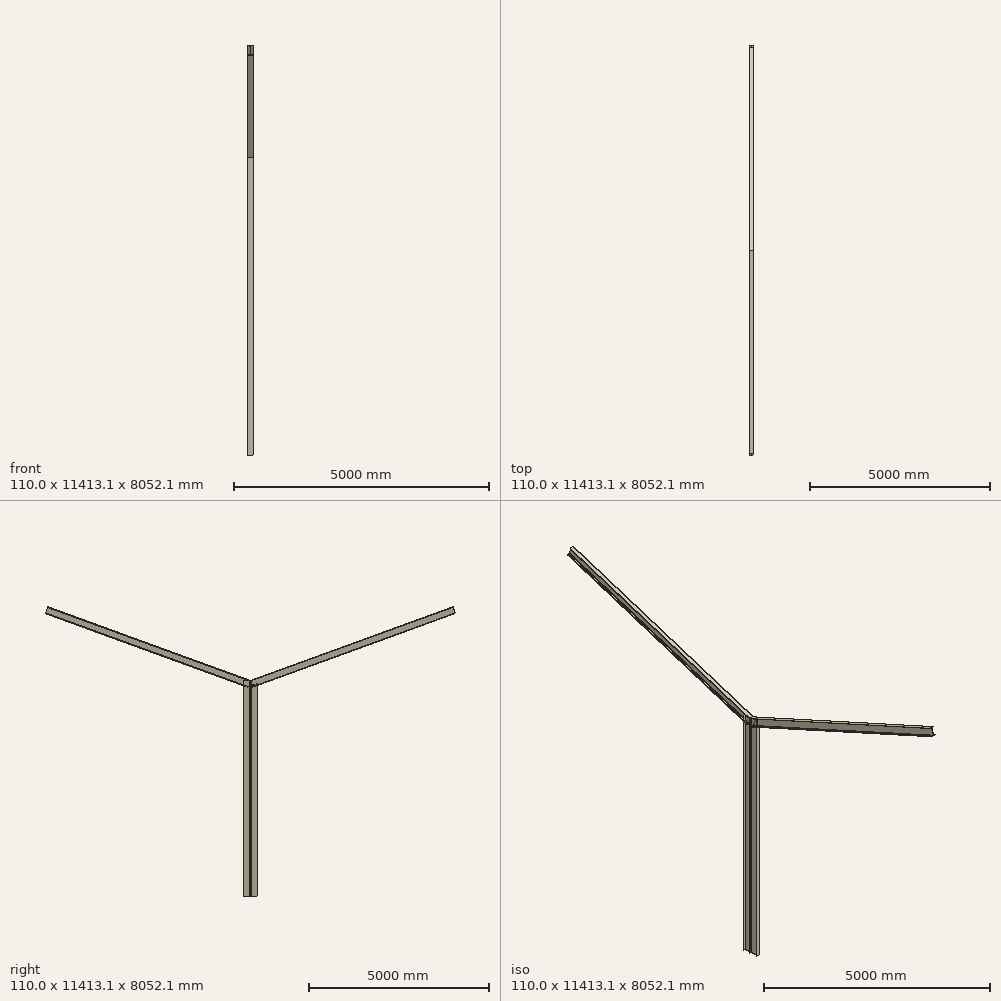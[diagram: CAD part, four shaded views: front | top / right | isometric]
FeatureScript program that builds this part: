
annotation { "Feature Type Name" : "Feature", "Feature Type Description" : "" }
export const myFeature = defineFeature(function(context is Context, id is Id, definition is map)
    precondition{}
    {
        {
            var Q0;
            Q0=qCreatedBy(makeId("Top.planeOp"),FACE);
            var sketch = newSketch(context, id + "F0", { "sketchPlane" : qUnion([Q0])});
            skLineSegment(sketch, "E0.bottom", {"start": v(0, 0) * mm, "end": v(-50, 0) * mm, "construction": true});
            skLineSegment(sketch, "E0.top", {"start": v(0, 100) * mm, "end": v(-55, 100) * mm});
            skLineSegment(sketch, "E0.left", {"start": v(0, 0) * mm, "end": v(0, 100) * mm, "construction": true});
            skLineSegment(sketch, "E0.right", {"start": v(-50, 0) * mm, "end": v(-50, 100) * mm, "construction": true});
            skCircle(sketch, "E1", {"center": v(-50, 100) * mm, "radius": 5 * mm});
            skLineSegment(sketch, "E2", {"start": v(-50.78, 95.06) * mm, "end": v(-9.06, 88.45) * mm});
            skLineSegment(sketch, "E3.MirrorCS", {"start": v(50.78, 95.06) * mm, "end": v(9.06, 88.45) * mm});
            skLineSegment(sketch, "E4.MirrorCS", {"start": v(0, 100) * mm, "end": v(55, 100) * mm});
            skCircle(sketch, "E5.MirrorC", {"center": v(50, 100) * mm, "radius": 5 * mm});
            skLineSegment(sketch, "E6.MirrorCS", {"start": v(-50.78, -95.06) * mm, "end": v(-9.06, -88.45) * mm});
            skLineSegment(sketch, "E7.MirrorCS", {"start": v(0, -100) * mm, "end": v(-55, -100) * mm});
            skLineSegment(sketch, "E8.MirrorCS", {"start": v(0, -100) * mm, "end": v(55, -100) * mm});
            skLineSegment(sketch, "E9.MirrorCS", {"start": v(50.78, -95.06) * mm, "end": v(9.06, -88.45) * mm});
            skCircle(sketch, "E10.MirrorC", {"center": v(-50, -100) * mm, "radius": 5 * mm});
            skCircle(sketch, "E11.MirrorC", {"center": v(50, -100) * mm, "radius": 5 * mm});
            skLineSegment(sketch, "E12", {"start": v(-4, 82.53) * mm, "end": v(-4, -82.53) * mm});
            skLineSegment(sketch, "E13", {"start": v(4, 82.53) * mm, "end": v(4, -82.53) * mm});
            skPoint(sketch, "E14.newPointA", {"position": v(0, 87.02) * mm});
            skArc(sketch, "E14.filletArc", {"start": v(-4, 82.53) * mm, "mid": v(-5.44, 86.42) * mm, "end": v(-9.06, 88.45) * mm});
            skArc(sketch, "E15.filletArc", {"start": v(9.06, 88.45) * mm, "mid": v(5.44, 86.42) * mm, "end": v(4, 82.53) * mm});
            skPoint(sketch, "E16.newPointA", {"position": v(0, -87.02) * mm});
            skArc(sketch, "E16.filletArc", {"start": v(-9.06, -88.45) * mm, "mid": v(-5.44, -86.42) * mm, "end": v(-4, -82.53) * mm});
            skArc(sketch, "E17.filletArc", {"start": v(4, -82.53) * mm, "mid": v(5.44, -86.42) * mm, "end": v(9.06, -88.45) * mm});
            skSolve(sketch);
        }
        {
            var Q0;
            {var subQ13=sQuery(id+"F0.wireOp",EDGE,"E2");Q0=makeQuery(id+"F0.imprint","IMPRINT",FACE,{"disambiguationData":[TD([[makeQuery(id+"F0.imprint","IMPRINT",EDGE,{"derivedFrom":subQ13}),1.0]])]});}
            var Q1;
            {var subQ0=sQuery(id+"F0.wireOp",EDGE,"E10.MirrorC");var subQ1=sQuery(id+"F0.wireOp",EDGE,"E7.MirrorCS");var subQ2=makeQuery(id+"F0.imprint","INTERSECT",VERTEX,{"disambiguationData":[OD(0.0)],"derivedFrom":[subQ1,subQ0]});Q1=makeQuery(id+"F0.imprint","IMPRINT",FACE,{"disambiguationData":[TD([[makeQuery(id+"F0.imprint","IMPRINT",EDGE,{"disambiguationData":[TD([[subQ2,1.0]])],"derivedFrom":subQ1}),-1.0]])]});}
            var Q2;
            {var subQ0=sQuery(id+"F0.wireOp",EDGE,"E11.MirrorC");var subQ1=sQuery(id+"F0.wireOp",EDGE,"E8.MirrorCS");var subQ2=makeQuery(id+"F0.imprint","INTERSECT",VERTEX,{"disambiguationData":[OD(0.0)],"derivedFrom":[subQ1,subQ0]});Q2=makeQuery(id+"F0.imprint","IMPRINT",FACE,{"disambiguationData":[TD([[makeQuery(id+"F0.imprint","IMPRINT",EDGE,{"disambiguationData":[TD([[subQ2,1.0]])],"derivedFrom":subQ1}),1.0]])]});}
            var Q3;
            {var subQ0=sQuery(id+"F0.wireOp",EDGE,"E1");var subQ1=sQuery(id+"F0.wireOp",EDGE,"E0.top");var subQ2=makeQuery(id+"F0.imprint","INTERSECT",VERTEX,{"disambiguationData":[OD(0.0)],"derivedFrom":[subQ1,subQ0]});Q3=makeQuery(id+"F0.imprint","IMPRINT",FACE,{"disambiguationData":[TD([[makeQuery(id+"F0.imprint","IMPRINT",EDGE,{"disambiguationData":[TD([[subQ2,1.0]])],"derivedFrom":subQ1}),1.0]])]});}
            var Q4;
            {var subQ0=sQuery(id+"F0.wireOp",EDGE,"E5.MirrorC");var subQ1=sQuery(id+"F0.wireOp",EDGE,"E4.MirrorCS");var subQ2=makeQuery(id+"F0.imprint","INTERSECT",VERTEX,{"disambiguationData":[OD(0.0)],"derivedFrom":[subQ1,subQ0]});Q4=makeQuery(id+"F0.imprint","IMPRINT",FACE,{"disambiguationData":[TD([[makeQuery(id+"F0.imprint","IMPRINT",EDGE,{"disambiguationData":[TD([[subQ2,1.0]])],"derivedFrom":subQ1}),-1.0]])]});}
            extrude(context, id + "F2", {"entities" : qUnion([Q0, Q1, Q2, Q3, Q4]), "depth" : 6000 * mm});
        }
        {
            var Q0;
            Q0=makeQuery(id+"F2.opExtrude","SWEPT_BODY",BODY,{"disambiguationData":[OSD([sQuery(id+"F0.wireOp",EDGE,"E0.top"),sQuery(id+"F0.wireOp",EDGE,"E1"),sQuery(id+"F0.wireOp",EDGE,"E2"),sQuery(id+"F0.wireOp",EDGE,"E3.MirrorCS"),sQuery(id+"F0.wireOp",EDGE,"E4.MirrorCS"),sQuery(id+"F0.wireOp",EDGE,"E5.MirrorC"),sQuery(id+"F0.wireOp",EDGE,"E6.MirrorCS"),sQuery(id+"F0.wireOp",EDGE,"E7.MirrorCS"),sQuery(id+"F0.wireOp",EDGE,"E8.MirrorCS"),sQuery(id+"F0.wireOp",EDGE,"E9.MirrorCS"),sQuery(id+"F0.wireOp",EDGE,"E10.MirrorC"),sQuery(id+"F0.wireOp",EDGE,"E11.MirrorC"),sQuery(id+"F0.wireOp",EDGE,"E12"),sQuery(id+"F0.wireOp",EDGE,"E13"),sQuery(id+"F0.wireOp",EDGE,"E14.filletArc"),sQuery(id+"F0.wireOp",EDGE,"E15.filletArc"),sQuery(id+"F0.wireOp",EDGE,"E16.filletArc"),sQuery(id+"F0.wireOp",EDGE,"E17.filletArc")])]});
            var Q1;
            Q1=makeQuery(id+"F2.opExtrude","CAP_EDGE",EDGE,{"disambiguationData":[OSD([sQuery(id+"F0.wireOp",EDGE,"E0.top"),sQuery(id+"F0.wireOp",EDGE,"E4.MirrorCS")])],"isStart":false});
            transform(context, id + "F1", {"entities" : qUnion([Q0]), "transformType" : TransformType.ROTATION, "transformAxis" : qUnion([Q1]), "angle" : 110 * degree, "makeCopy" : true});
        }
        {
            var Q0;
            Q0=makeQuery(id+"F1.opPattern","COPY",BODY,{"derivedFrom":makeQuery(id+"F2.opExtrude","SWEPT_BODY",BODY,{"disambiguationData":[OSD([sQuery(id+"F0.wireOp",EDGE,"E0.top"),sQuery(id+"F0.wireOp",EDGE,"E1"),sQuery(id+"F0.wireOp",EDGE,"E2"),sQuery(id+"F0.wireOp",EDGE,"E3.MirrorCS"),sQuery(id+"F0.wireOp",EDGE,"E4.MirrorCS"),sQuery(id+"F0.wireOp",EDGE,"E5.MirrorC"),sQuery(id+"F0.wireOp",EDGE,"E6.MirrorCS"),sQuery(id+"F0.wireOp",EDGE,"E7.MirrorCS"),sQuery(id+"F0.wireOp",EDGE,"E8.MirrorCS"),sQuery(id+"F0.wireOp",EDGE,"E9.MirrorCS"),sQuery(id+"F0.wireOp",EDGE,"E10.MirrorC"),sQuery(id+"F0.wireOp",EDGE,"E11.MirrorC"),sQuery(id+"F0.wireOp",EDGE,"E12"),sQuery(id+"F0.wireOp",EDGE,"E13"),sQuery(id+"F0.wireOp",EDGE,"E14.filletArc"),sQuery(id+"F0.wireOp",EDGE,"E15.filletArc"),sQuery(id+"F0.wireOp",EDGE,"E16.filletArc"),sQuery(id+"F0.wireOp",EDGE,"E17.filletArc")])]}),"instanceName":"1"});
            var Q1;
            Q1=makeQuery(id+"F2.opExtrude","SWEPT_BODY",BODY,{"disambiguationData":[OSD([sQuery(id+"F0.wireOp",EDGE,"E0.top"),sQuery(id+"F0.wireOp",EDGE,"E1"),sQuery(id+"F0.wireOp",EDGE,"E2"),sQuery(id+"F0.wireOp",EDGE,"E3.MirrorCS"),sQuery(id+"F0.wireOp",EDGE,"E4.MirrorCS"),sQuery(id+"F0.wireOp",EDGE,"E5.MirrorC"),sQuery(id+"F0.wireOp",EDGE,"E6.MirrorCS"),sQuery(id+"F0.wireOp",EDGE,"E7.MirrorCS"),sQuery(id+"F0.wireOp",EDGE,"E8.MirrorCS"),sQuery(id+"F0.wireOp",EDGE,"E9.MirrorCS"),sQuery(id+"F0.wireOp",EDGE,"E10.MirrorC"),sQuery(id+"F0.wireOp",EDGE,"E11.MirrorC"),sQuery(id+"F0.wireOp",EDGE,"E12"),sQuery(id+"F0.wireOp",EDGE,"E13"),sQuery(id+"F0.wireOp",EDGE,"E14.filletArc"),sQuery(id+"F0.wireOp",EDGE,"E15.filletArc"),sQuery(id+"F0.wireOp",EDGE,"E16.filletArc"),sQuery(id+"F0.wireOp",EDGE,"E17.filletArc")])]});
            var Q2;
            Q2=makeQuery(id+"F2.opExtrude","SWEPT_FACE",FACE,{"disambiguationData":[OSD([sQuery(id+"F0.wireOp",EDGE,"E0.top"),sQuery(id+"F0.wireOp",EDGE,"E4.MirrorCS")])]});
            mirror(context, id + "F3", {"entities" : qUnion([Q0, Q1]), "mirrorPlane" : qUnion([Q2])});
        }
    });
